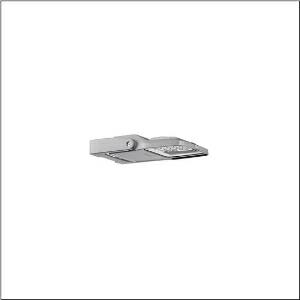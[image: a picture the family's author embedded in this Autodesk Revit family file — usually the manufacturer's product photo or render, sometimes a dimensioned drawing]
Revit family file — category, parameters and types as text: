
# Revit family: floodlight_fl_21_iq_micro___pl64_5xa7761a4e2a_05f9
name_source: partatom
category: Lighting Fixtures
units: mm (PartAtom-declared; Revit-internal decimal feet)

## family parameters
Cut with Voids When Loaded = No
Host = Face
Light Source = No
Part Type = Normal
Room Calculation Point = No
Round Connector Dimension = Use Diameter
Shared = No

## types (1)
- --- (1 x LED, 2980 lm, 23.1 W, 4000K)
    Apparent Load = 23 VA
    CIE Flux Codes = 28 80 98 100 100
    Color Rendering = 70
    Color Temperature = 4000K
    Default Elevation = 1800 mm
    Description = Floodlight FL 21 iQ micro, floodlight, primary light control with lens, of PMMA, primary optical cover: protective disc, of toughened safety glass, transparent, light distribution: PL64, light emission: direct distribution, installation type: surface-mounted, LED, High Power LED, rated luminous flux: 2.980lm, luminous efficacy: 129lm/W, light colour: 740, colour temperature: 4000K, control gear: iQ Comfort/DALI, control: optimised constant luminous flux control (CLO 2.0), Desk-Remote (wireless, voltage-free reading and setting of iQ features in the workshop via application-optimized NFC function/RFID function), Light-Fading, Smart-Wire, Night-Set, Lumen-Switch, Temp-Guard, Auto-Match, with terminal, 6-pole, mains connection: 220..240V, AC, 50/60Hz, start of lifetime: 23W, end of service life: 24W, reduction: 11W, luminaire housing, of diecast aluminium, powder-coated, Siteco® metallic grey (DB 702S), corrosivity category C5 mid according to DIN EN ISO 12944, suitable for swimming pools, chlorine-resistant, sealing non-destructively replaceable, design bracket, of diecast aluminium, powder-coated, Siteco® metallic grey (DB 702S), protection rating (complete): IP66, insulation class (complete): insulation class II (safety insulation), certification: CE, ENEC, VDE, protection symbol: D, impact resistance: IK07, permissible operating ambient temperature: -40..+40°C, permissible operating ambient temperature for outdoor applications: -40..+50°C, standard: DIN EN 12944, LABS conformity tested according to VDMA 24364:2018-05, packaging unit: 1 piece

Light Distribution: PL64
    Height = 65 mm
    Lamp = 1 x LED
    Lamp Light Flux = 2980 lm
    Lamp Power = 23.1 W
    Lamp count = 1
    Length = 312 mm
    Luminous efficacy = 129 lm/W
    Manufacturer = Siteco
    ModVariant = No
    Model = 5XA7761A4E2A
    Mounting Place = Wall
    Mounting Type = Surface mounted
    Number of Poles = 1
    OnlyDefault = Yes
    Power Factor = 1
    Product Name = Floodlight FL 21 iQ micro | PL64
    Product group = floodlight | wall mounted
    ProductGroupID = 2001
    Protection Class = Protection class II
    Protection Degree = IP 66
    RLX_Detail_Level = 1
    RLX_Emergency_Light_Flux = 0 lm
    RLX_Emergency_Type = 0
    RLX_Emergency_Type_DB = No
    RlxData = <blob elided: 97533 chars, md5=6a90e5f2>
    Socket = socket
    Standby Power = 0 W
    System Light Flux = 2980 lm
    System Power = 23 W
    Type Comments = factory setting: luminous flux: 100 % | dim-lin: 254 | 455 mA
    Type Image = l_1006878.jpg
    URL = http://relux.com
    VarID = @adj_180758
    Voltage = 0 V
    Weight = 0.00 kg
    Width = 230 mm

## geometry (parser evidence)
native form markers: Blend x4, Sweep x13
no freeform markers — native parametric forms only
